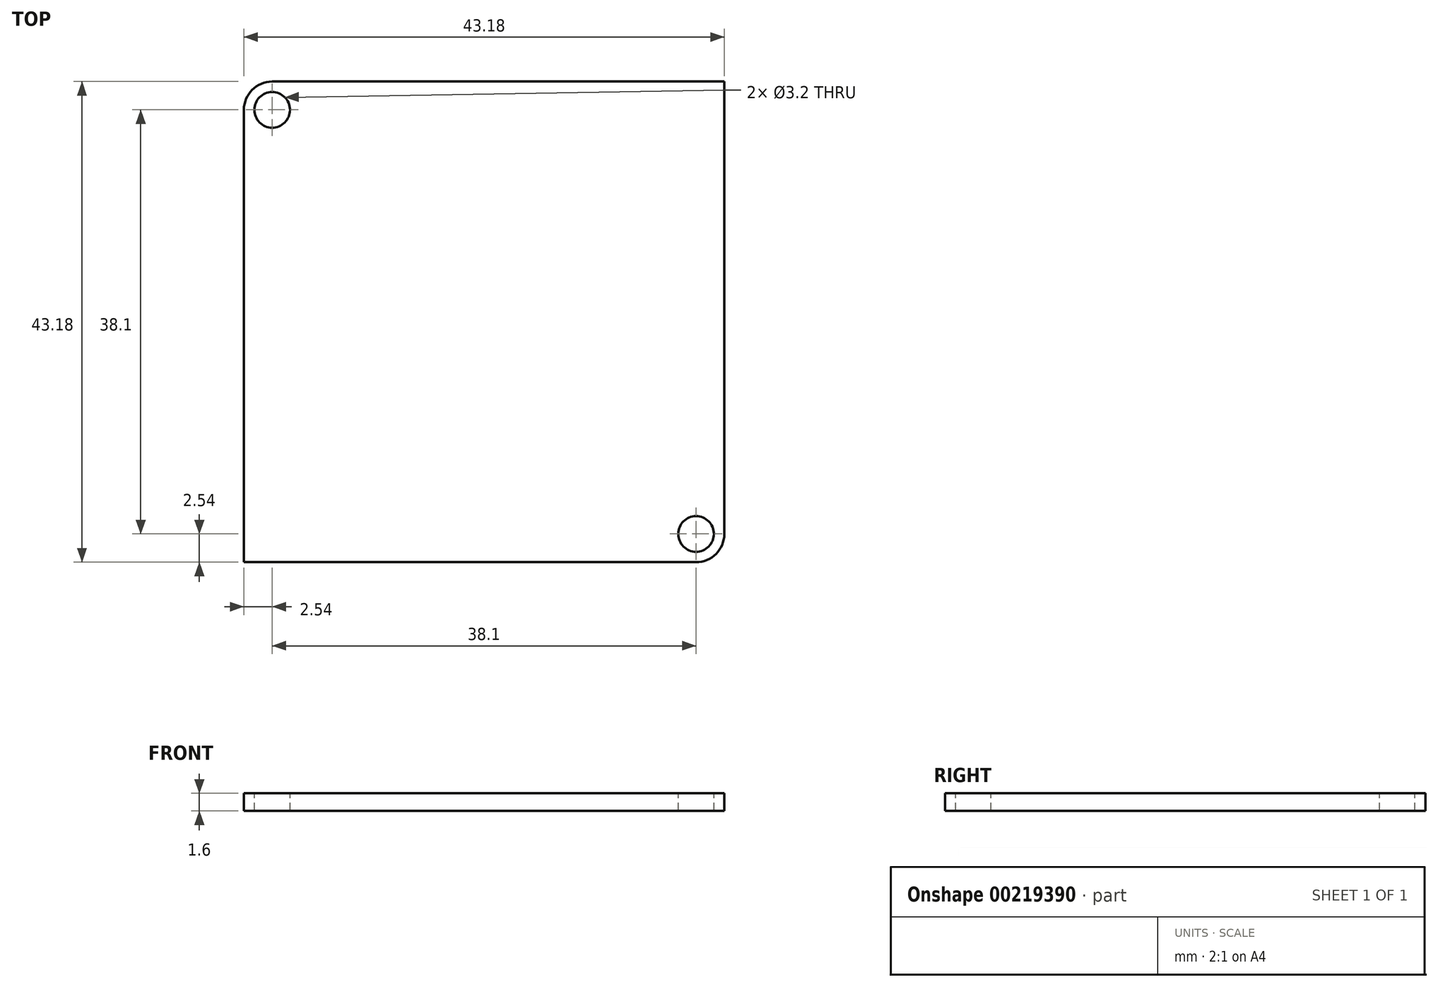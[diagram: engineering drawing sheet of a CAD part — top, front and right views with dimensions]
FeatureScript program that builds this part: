
annotation { "Feature Type Name" : "Feature", "Feature Type Description" : "" }
export const myFeature = defineFeature(function(context is Context, id is Id, definition is map)
    precondition{}
    {
        {
            var Q0;
            Q0=qCreatedBy(makeId("Top.planeOp"),FACE);
            var sketch = newSketch(context, id + "F0", { "sketchPlane" : qUnion([Q0])});
            skLineSegment(sketch, "E0.bottom", {"start": v(-19.05, 21.6) * mm, "end": v(21.6, 21.59) * mm});
            skLineSegment(sketch, "E0.top", {"start": v(-21.59, -21.59) * mm, "end": v(19.05, -21.6) * mm});
            skLineSegment(sketch, "E0.left", {"start": v(-21.59, 19.05) * mm, "end": v(-21.59, -21.59) * mm});
            skLineSegment(sketch, "E0.right", {"start": v(21.6, 21.59) * mm, "end": v(21.59, -19.05) * mm});
            skPoint(sketch, "E1", {"position": v(0, 21.59) * mm});
            skPoint(sketch, "E2", {"position": v(-21.59, 0) * mm});
            skPoint(sketch, "E3.visualSharp", {"position": v(-21.6, 21.6) * mm});
            skArc(sketch, "E3.filletArc", {"start": v(-19.05, 21.6) * mm, "mid": v(-20.85, 20.85) * mm, "end": v(-21.6, 19.05) * mm});
            skPoint(sketch, "E4.visualSharp", {"position": v(21.6, -21.6) * mm});
            skArc(sketch, "E4.filletArc", {"start": v(19.05, -21.59) * mm, "mid": v(20.85, -20.85) * mm, "end": v(21.6, -19.05) * mm});
            skCircle(sketch, "E5", {"center": v(-19.05, 19.05) * mm, "radius": 1.6 * mm});
            skCircle(sketch, "E6", {"center": v(19.05, -19.05) * mm, "radius": 1.6 * mm});
            skSolve(sketch);
        }
        {
            var Q0;
            Q0=makeQuery(id+"F0.imprint","IMPRINT",FACE,{"disambiguationData":[TD([[makeQuery(id+"F0.imprint","IMPRINT",EDGE,{"derivedFrom":sQuery(id+"F0.wireOp",EDGE,"E0.bottom")}),-1.0]])]});
            extrude(context, id + "F1", {"entities" : qUnion([Q0]), "oppositeDirection" : true, "depth" : 1.6 * mm});
        }
    });
